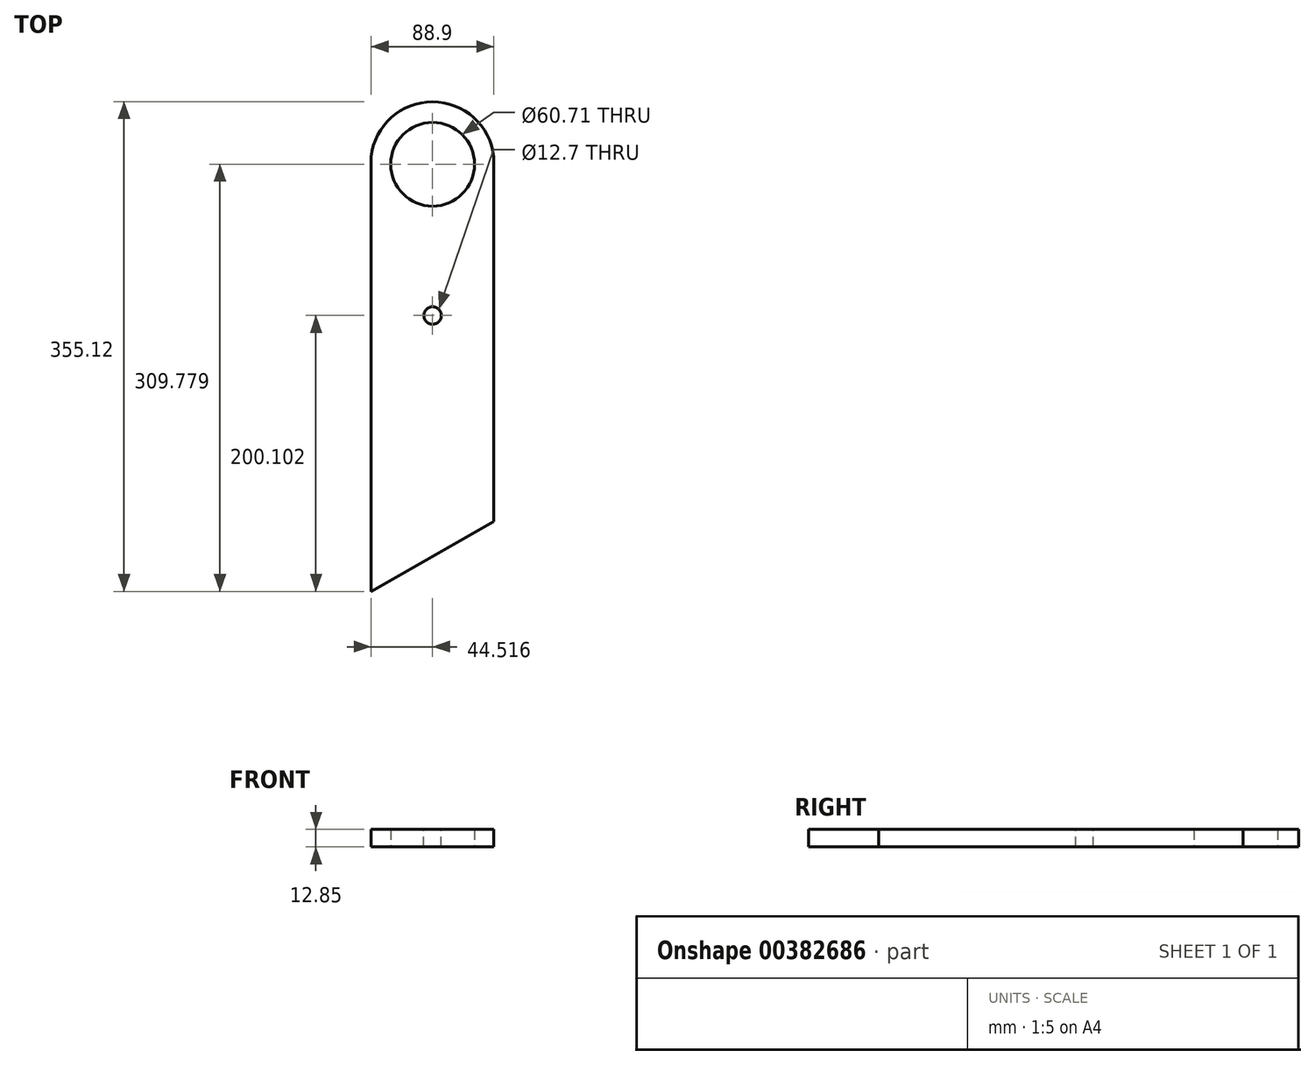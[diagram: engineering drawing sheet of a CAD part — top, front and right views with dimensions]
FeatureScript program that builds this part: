
annotation { "Feature Type Name" : "Feature", "Feature Type Description" : "" }
export const myFeature = defineFeature(function(context is Context, id is Id, definition is map)
    precondition{}
    {
        {
            var Q0;
            Q0=qCreatedBy(makeId("Top.planeOp"),FACE);
            var sketch = newSketch(context, id + "F0", { "sketchPlane" : qUnion([Q0])});
            skLineSegment(sketch, "E0.bottom", {"start": v(-21.34, -167.78) * mm, "end": v(-110.24, -167.78) * mm});
            skLineSegment(sketch, "E0.top", {"start": v(-21.34, 187.82) * mm, "end": v(-110.24, 187.82) * mm});
            skLineSegment(sketch, "E0.left", {"start": v(-21.34, -167.78) * mm, "end": v(-21.34, 187.82) * mm});
            skLineSegment(sketch, "E0.right", {"start": v(-110.24, -167.78) * mm, "end": v(-110.24, 187.82) * mm});
            skSolve(sketch);
        }
        {
            var Q0;
            Q0=makeQuery(id+"F0.imprint","IMPRINT",FACE,{"disambiguationData":[TD([[makeQuery(id+"F0.imprint","IMPRINT",EDGE,{"derivedFrom":sQuery(id+"F0.wireOp",EDGE,"E0.bottom")}),-1.0]])]});
            var sketch = newSketch(context, id + "F1", { "sketchPlane" : qUnion([Q0])});
            skCircle(sketch, "E1", {"center": v(-65.72, 142) * mm, "radius": 30.35 * mm});
            skSolve(sketch);
        }
        {
            var Q0;
            Q0=makeQuery(id+"F0.imprint","IMPRINT",FACE,{"disambiguationData":[TD([[makeQuery(id+"F0.imprint","IMPRINT",EDGE,{"derivedFrom":sQuery(id+"F0.wireOp",EDGE,"E0.bottom")}),-1.0]])]});
            var sketch = newSketch(context, id + "F2", { "sketchPlane" : qUnion([Q0])});
            skLineSegment(sketch, "E2.0.0", {"start": v(-21.34, -167.78) * mm, "end": v(-21.34, 187.82) * mm});
            skLineSegment(sketch, "E2.0.2", {"start": v(-110.24, 187.82) * mm, "end": v(-110.24, -167.78) * mm});
            skLineSegment(sketch, "E2.0.3", {"start": v(-110.24, -167.78) * mm, "end": v(-21.34, -167.78) * mm});
            skArc(sketch, "E3", {"start": v(-21.34, 147.3) * mm, "mid": v(-65.79, 187.34) * mm, "end": v(-110.24, 147.3) * mm});
            skSolve(sketch);
        }
        {
            var Q0;
            Q0=makeQuery(id+"F1.imprint","IMPRINT",FACE,{"disambiguationData":[TD([[makeQuery(id+"F1.imprint","IMPRINT",EDGE,{"derivedFrom":sQuery(id+"F1.wireOp",EDGE,"E1")}),-1.0]])]});
            var sketch = newSketch(context, id + "F3", { "sketchPlane" : qUnion([Q0])});
            skArc(sketch, "E4.0", {"start": v(-21.34, 147.3) * mm, "mid": v(-65.79, 187.34) * mm, "end": v(-110.24, 147.3) * mm});
            skCircle(sketch, "E5.0", {"center": v(-65.72, 142) * mm, "radius": 30.35 * mm});
            skLineSegment(sketch, "E6.0", {"start": v(-110.24, -167.78) * mm, "end": v(-110.24, 187.82) * mm});
            skLineSegment(sketch, "E7.0", {"start": v(-21.34, -167.78) * mm, "end": v(-21.34, 187.82) * mm});
            skLineSegment(sketch, "E8.0", {"start": v(-21.34, -167.78) * mm, "end": v(-110.24, -167.78) * mm});
            skSolve(sketch);
        }
        {
            var Q0;
            {var subQ2=sQuery(id+"F3.wireOp",EDGE,"E4.0");Q0=makeQuery(id+"F3.imprint","IMPRINT",FACE,{"disambiguationData":[TD([[makeQuery(id+"F3.imprint","IMPRINT",EDGE,{"derivedFrom":subQ2}),1.0]])]});}
            var sketch = newSketch(context, id + "F4", { "sketchPlane" : qUnion([Q0])});
            skArc(sketch, "E9.0.1", {"start": v(-21.34, 147.3) * mm, "mid": v(-65.79, 187.34) * mm, "end": v(-110.24, 147.3) * mm});
            skLineSegment(sketch, "E10", {"start": v(-110.24, -167.78) * mm, "end": v(-21.34, -116.98) * mm});
            skSolve(sketch);
        }
        {
            var Q0;
            {var subQ4=sQuery(id+"F4.wireOp",EDGE,"E9.0.1");Q0=makeQuery(id+"F4.imprint","IMPRINT",FACE,{"disambiguationData":[TD([[makeQuery(id+"F4.imprint","IMPRINT",EDGE,{"derivedFrom":subQ4}),1.0]])]});}
            var sketch = newSketch(context, id + "F5", { "sketchPlane" : qUnion([Q0])});
            skLineSegment(sketch, "E11.0.0", {"start": v(-110.24, 147.3) * mm, "end": v(-110.24, -167.78) * mm});
            skLineSegment(sketch, "E11.0.1", {"start": v(-110.24, -167.78) * mm, "end": v(-21.34, -116.98) * mm});
            skLineSegment(sketch, "E11.0.2", {"start": v(-21.34, -116.98) * mm, "end": v(-21.34, 147.3) * mm});
            skArc(sketch, "E11.0.3", {"start": v(-21.34, 147.3) * mm, "mid": v(-65.79, 187.34) * mm, "end": v(-110.24, 147.3) * mm});
            skCircle(sketch, "E12.0", {"center": v(-65.72, 142) * mm, "radius": 30.35 * mm});
            skSolve(sketch);
        }
        {
            var Q0;
            {var subQ4=sQuery(id+"F4.wireOp",EDGE,"E9.0.1");Q0=makeQuery(id+"F4.imprint","IMPRINT",FACE,{"disambiguationData":[TD([[makeQuery(id+"F4.imprint","IMPRINT",EDGE,{"derivedFrom":subQ4}),1.0]])]});}
            extrude(context, id + "F6", {"entities" : qUnion([Q0]), "depth" : 12.85 * mm});
        }
        {
            var Q0;
            Q0=makeQuery(id+"F6.opExtrude","CAP_FACE",FACE,{"disambiguationData":[OSD([sQuery(id+"F3.wireOp",EDGE,"E5.0"),sQuery(id+"F3.wireOp",EDGE,"E6.0"),sQuery(id+"F3.wireOp",EDGE,"E7.0"),sQuery(id+"F4.wireOp",EDGE,"E9.0.1"),sQuery(id+"F4.wireOp",EDGE,"E10")])],"isStart":false});
            var sketch = newSketch(context, id + "F7", { "sketchPlane" : qUnion([Q0])});
            skLineSegment(sketch, "E13", {"start": v(-65.72, 142) * mm, "end": v(-65.72, 32.32) * mm});
            skCircle(sketch, "E14", {"center": v(-65.72, 32.32) * mm, "radius": 6.35 * mm});
            skSolve(sketch);
        }
        {
            var Q0;
            Q0=makeQuery(id+"F7.imprint","IMPRINT",FACE,{"disambiguationData":[TD([[makeQuery(id+"F7.imprint","IMPRINT",EDGE,{"derivedFrom":sQuery(id+"F7.wireOp",EDGE,"E14")}),1.0]])]});
            extrude(context, id + "F8", {"entities" : qUnion([Q0]), "operationType" : NewBodyOperationType.REMOVE, "oppositeDirection" : true, "depth" : 25.4 * mm});
        }
    });
